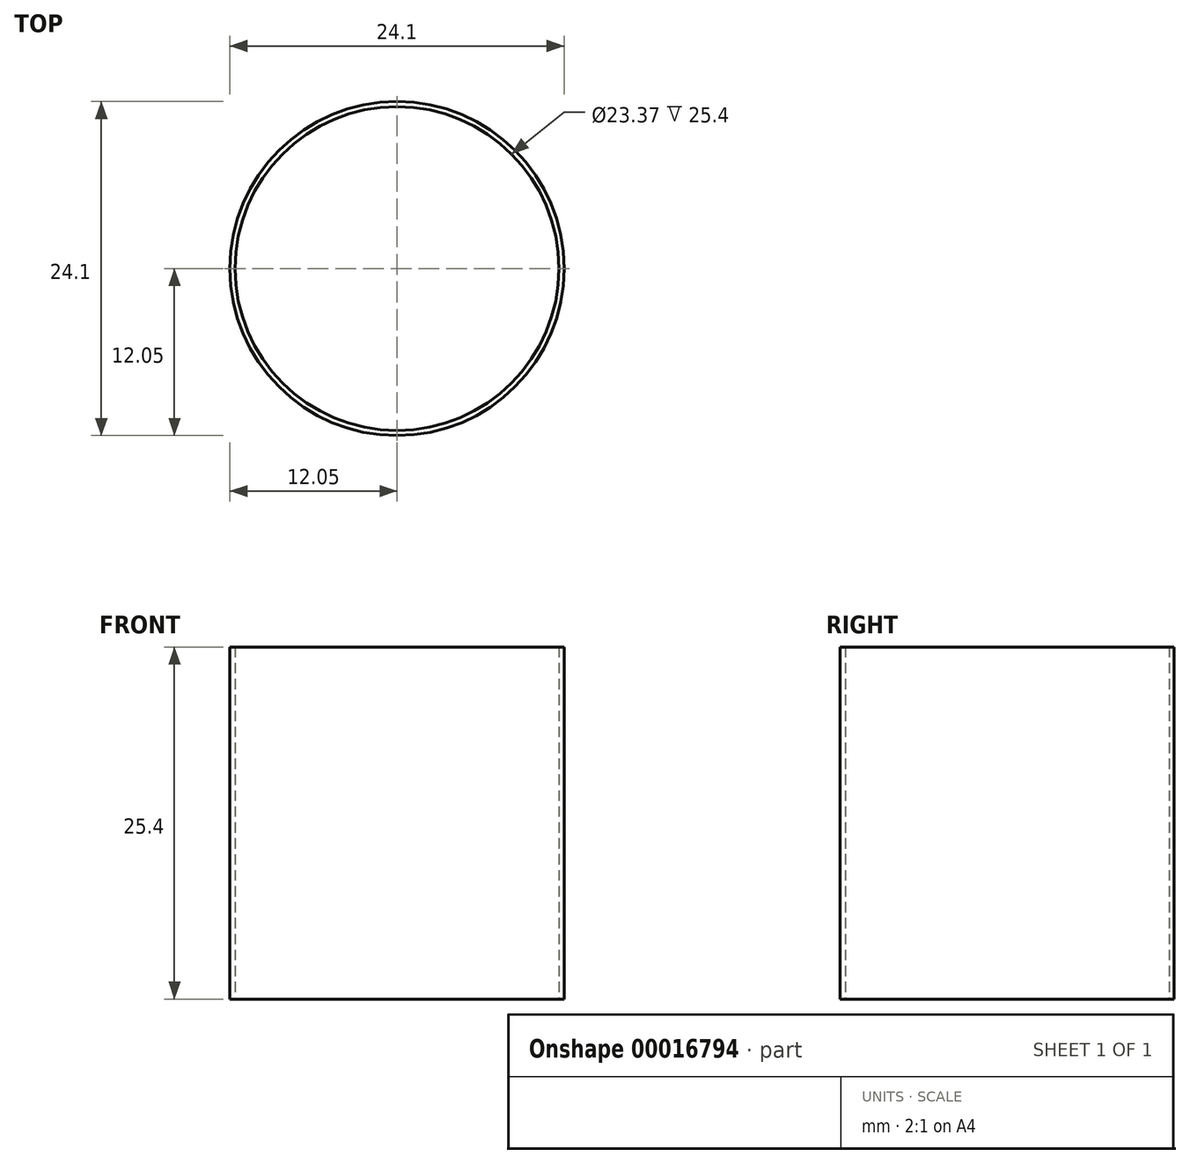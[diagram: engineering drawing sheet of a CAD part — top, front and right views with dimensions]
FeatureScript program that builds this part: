
annotation { "Feature Type Name" : "Feature", "Feature Type Description" : "" }
export const myFeature = defineFeature(function(context is Context, id is Id, definition is map)
    precondition{}
    {
        {
            var Q0;
            Q0=qCreatedBy(makeId("Front.planeOp"),FACE);
            var sketch = newSketch(context, id + "F0", { "sketchPlane" : qUnion([Q0])});
            skLineSegment(sketch, "E0", {"start": v(0, 0) * mm, "end": v(0, 25.4) * mm});
            skLineSegment(sketch, "E1", {"start": v(0, 25.4) * mm, "end": v(11.68, 25.4) * mm});
            skLineSegment(sketch, "E2", {"start": v(11.68, 25.4) * mm, "end": v(11.68, 0) * mm});
            skLineSegment(sketch, "E3", {"start": v(11.68, 0) * mm, "end": v(0, 0) * mm});
            skLineSegment(sketch, "E4", {"start": v(11.68, 0) * mm, "end": v(12.05, 0) * mm});
            skLineSegment(sketch, "E5", {"start": v(12.05, 0) * mm, "end": v(12.05, 25.4) * mm});
            skLineSegment(sketch, "E6", {"start": v(12.05, 25.4) * mm, "end": v(11.68, 25.4) * mm});
            skSolve(sketch);
        }
        {
            var Q0;
            Q0=makeQuery(id+"F0.imprint","IMPRINT",FACE,{"disambiguationData":[TD([[makeQuery(id+"F0.imprint","IMPRINT",EDGE,{"derivedFrom":sQuery(id+"F0.wireOp",EDGE,"E2")}),1.0]])]});
            var Q1;
            Q1=sQuery(id+"F0.wireOp",EDGE,"E0");
            revolve(context, id + "F1", {"entities" : qUnion([Q0]), "axis" : qUnion([Q1]), "revolveType" : RevolveType.FULL});
        }
    });
